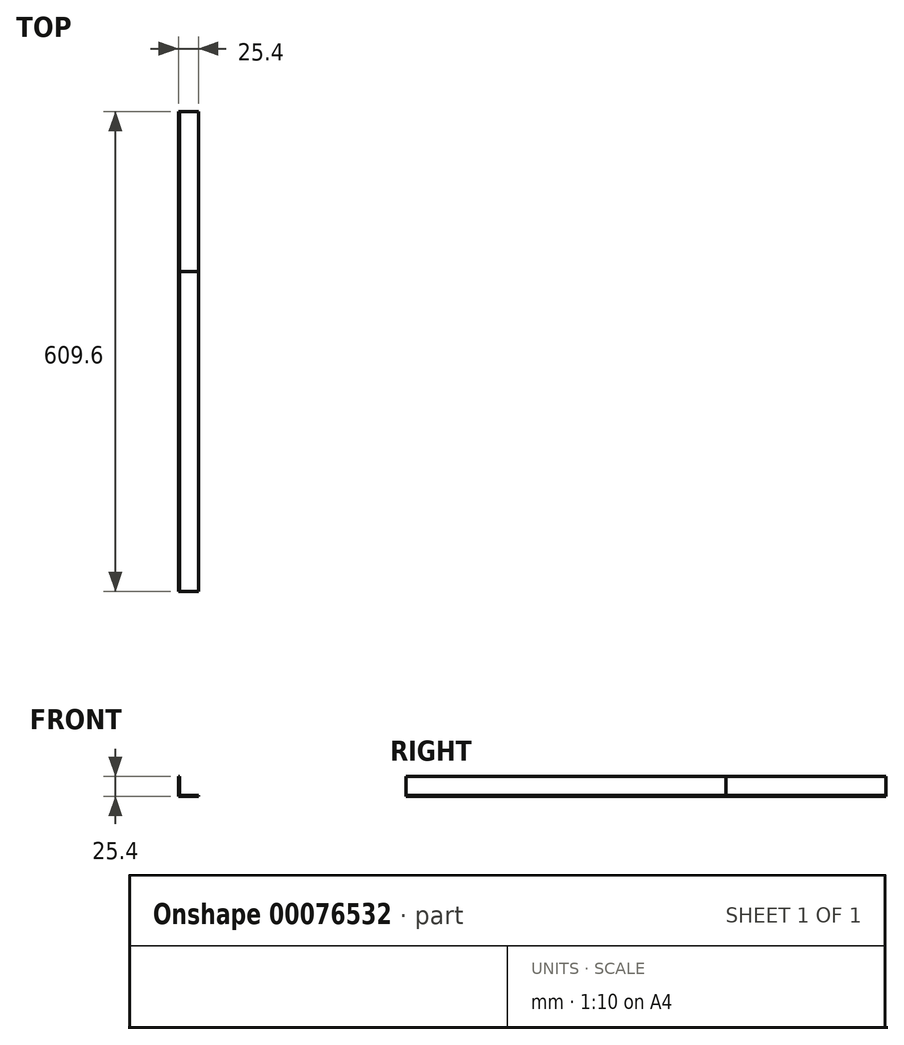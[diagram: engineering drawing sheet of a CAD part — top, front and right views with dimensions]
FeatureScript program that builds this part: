
annotation { "Feature Type Name" : "Feature", "Feature Type Description" : "" }
export const myFeature = defineFeature(function(context is Context, id is Id, definition is map)
    precondition{}
    {
        {
            var Q0;
            Q0=qCreatedBy(makeId("Front.planeOp"),FACE);
            var sketch = newSketch(context, id + "F0", { "sketchPlane" : qUnion([Q0])});
            skLineSegment(sketch, "E0", {"start": v(0, 0) * mm, "end": v(0, 25.4) * mm});
            skLineSegment(sketch, "E1", {"start": v(0, 25.4) * mm, "end": v(1.59, 25.4) * mm});
            skLineSegment(sketch, "E2", {"start": v(1.59, 25.4) * mm, "end": v(1.59, 1.59) * mm});
            skLineSegment(sketch, "E3", {"start": v(1.59, 1.59) * mm, "end": v(25.4, 1.59) * mm});
            skLineSegment(sketch, "E4", {"start": v(25.4, 1.59) * mm, "end": v(25.4, 0) * mm});
            skLineSegment(sketch, "E5", {"start": v(25.4, 0) * mm, "end": v(0, 0) * mm});
            skSolve(sketch);
        }
        {
            var Q0;
            Q0=makeQuery(id+"F0.imprint","IMPRINT",FACE,{"disambiguationData":[TD([[makeQuery(id+"F0.imprint","IMPRINT",EDGE,{"derivedFrom":sQuery(id+"F0.wireOp",EDGE,"E0")}),-1.0]])]});
            extrude(context, id + "F1", {"entities" : qUnion([Q0]), "depth" : 203.2 * mm});
        }
        {
            var Q0;
            Q0=qSketchRegion(id+"F0",true);
            extrude(context, id + "F2", {"entities" : qUnion([Q0]), "depth" : 609.6 * mm});
        }
    });
